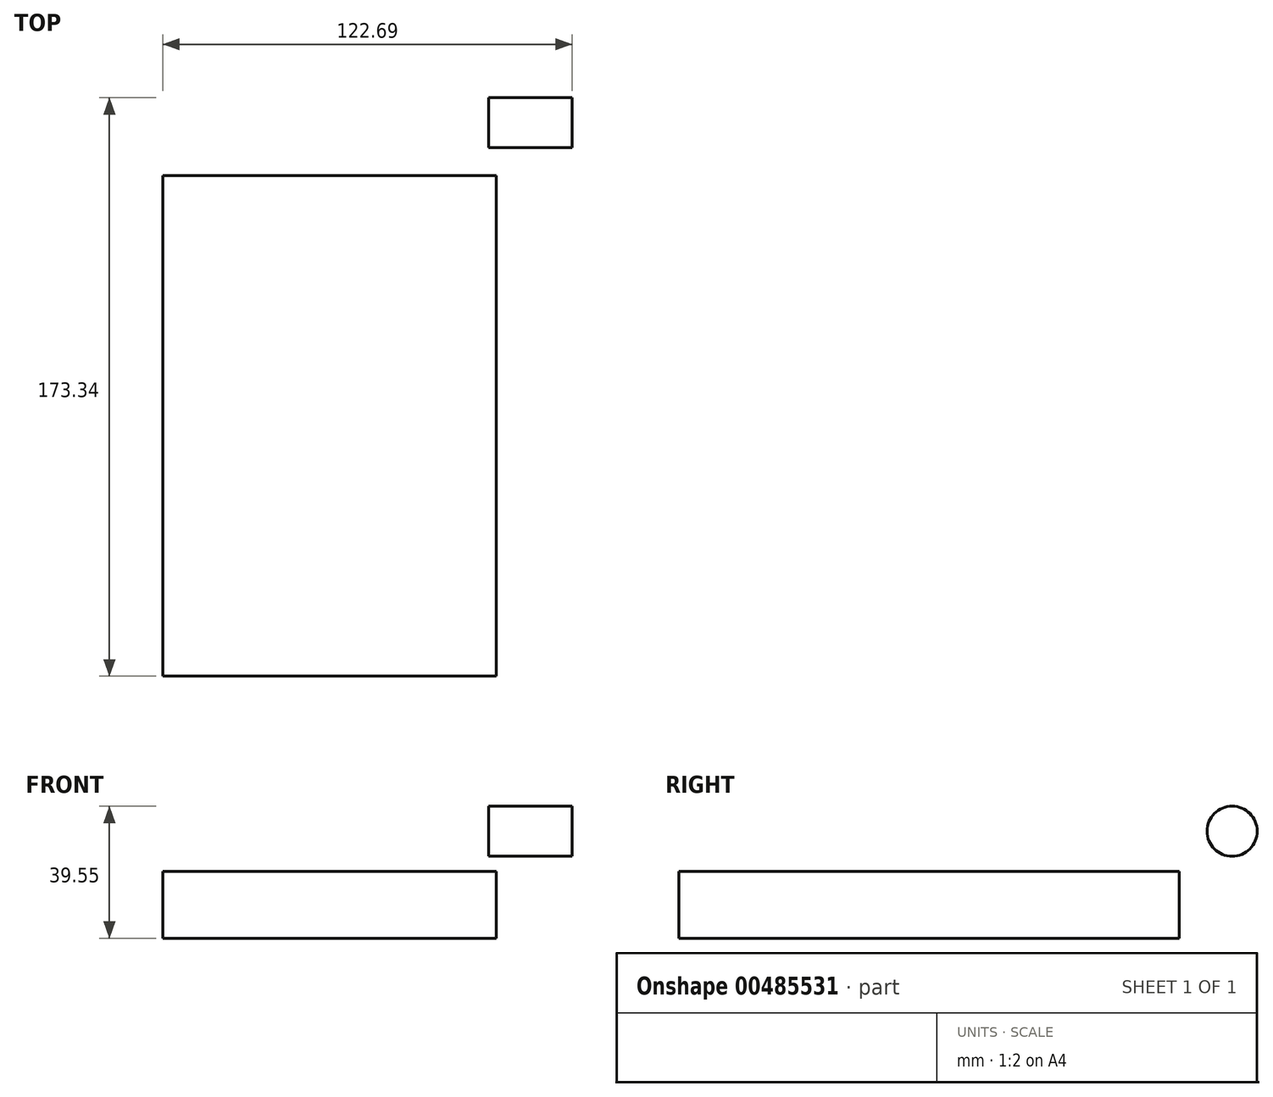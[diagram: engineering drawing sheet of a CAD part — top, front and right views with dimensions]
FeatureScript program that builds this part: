
annotation { "Feature Type Name" : "Feature", "Feature Type Description" : "" }
export const myFeature = defineFeature(function(context is Context, id is Id, definition is map)
    precondition{}
    {
        {
            var Q0;
            Q0=qCreatedBy(makeId("Top.planeOp"),FACE);
            var sketch = newSketch(context, id + "F0", { "sketchPlane" : qUnion([Q0])});
            skLineSegment(sketch, "E0.bottom", {"start": v(2.31, 42.01) * mm, "end": v(-97.69, 42.01) * mm});
            skLineSegment(sketch, "E0.top", {"start": v(2.31, -107.99) * mm, "end": v(-97.69, -107.99) * mm});
            skLineSegment(sketch, "E0.left", {"start": v(2.31, 42.01) * mm, "end": v(2.31, -107.99) * mm});
            skLineSegment(sketch, "E0.right", {"start": v(-97.69, 42.01) * mm, "end": v(-97.69, -107.99) * mm});
            skSolve(sketch);
        }
        {
            var Q0;
            Q0 = qSketchRegion(id + "F0", true);
            var sketch = newSketch(context, id + "F1", { "sketchPlane" : qUnion([Q0])});
            skSolve(sketch);
        }
        {
            var Q0;
            Q0=makeQuery(id+"F1.imprint","IMPRINT",FACE,{"disambiguationData":[TD([[makeQuery(id+"F1.imprint","IMPRINT",EDGE,{"derivedFrom":makeQuery(id+"F0.imprint","IMPRINT",EDGE,{"derivedFrom":sQuery(id+"F0.wireOp",EDGE,"E0.bottom")})}),1.0]])]});
            extrude(context, id + "F2", {"entities" : qUnion([Q0]), "depth" : 20 * mm, "offsetDistance" : 25.4 * mm});
        }
        {
            var Q0;
            Q0=qCreatedBy(makeId("Right.planeOp"),FACE);
            var sketch = newSketch(context, id + "F3", { "sketchPlane" : qUnion([Q0])});
            skCircle(sketch, "E1", {"center": v(57.85, 32.05) * mm, "radius": 7.5 * mm});
            skSolve(sketch);
        }
        {
            var Q0;
            Q0 = qSketchRegion(id + "F3", true);
            extrude(context, id + "F4", {"entities" : qUnion([Q0]), "depth" : 25 * mm, "offsetDistance" : 25 * mm});
        }
    });
